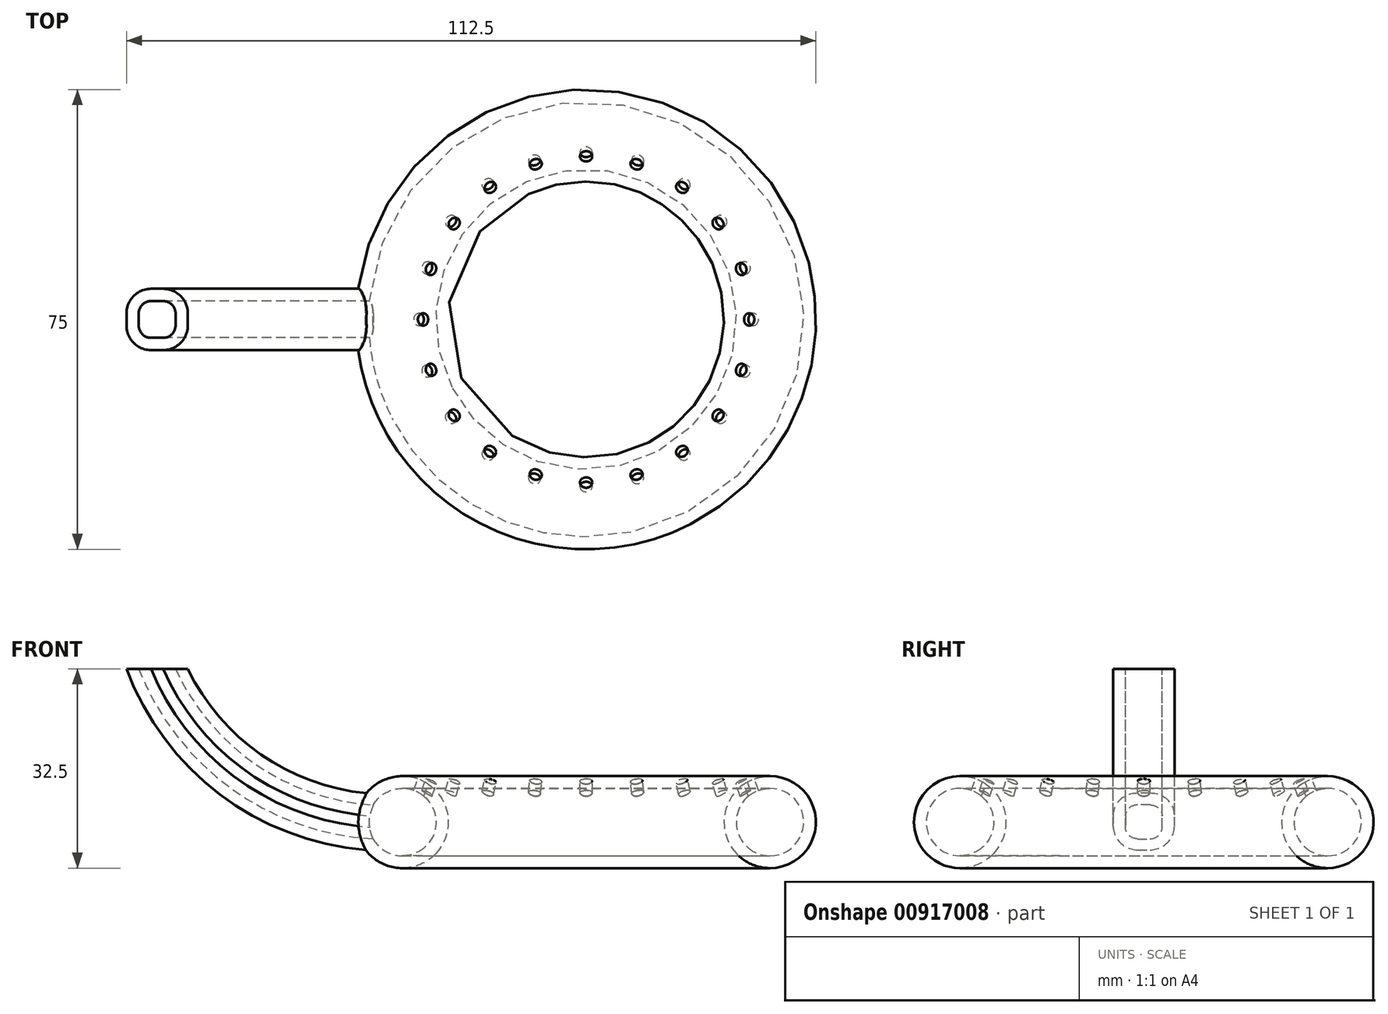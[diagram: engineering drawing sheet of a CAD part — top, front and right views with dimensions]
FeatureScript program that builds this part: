
annotation { "Feature Type Name" : "Feature", "Feature Type Description" : "" }
export const myFeature = defineFeature(function(context is Context, id is Id, definition is map)
    precondition{}
    {
        {
            var Q0;
            Q0=qCreatedBy(makeId("Front.planeOp"),FACE);
            var sketch = newSketch(context, id + "F0", { "sketchPlane" : qUnion([Q0])});
            skCircle(sketch, "E0", {"center": v(-30, 0) * mm, "radius": 7.5 * mm});
            skCircle(sketch, "E1", {"center": v(-30, 0) * mm, "radius": 5.5 * mm});
            skLineSegment(sketch, "E2", {"start": v(0, 0) * mm, "end": v(0, 9.49) * mm});
            skSolve(sketch);
        }
        {
            var Q0;
            Q0=makeQuery(id+"F0.imprint","IMPRINT",FACE,{"disambiguationData":[TD([[makeQuery(id+"F0.imprint","IMPRINT",EDGE,{"derivedFrom":sQuery(id+"F0.wireOp",EDGE,"E0")}),1.0]])]});
            var Q1;
            Q1=sQuery(id+"F0.wireOp",EDGE,"E2");
            revolve(context, id + "F1", {"surfaceOperationType" : NewSurfaceOperationType.NEW, "entities" : qUnion([Q0]), "axis" : qUnion([Q1]), "revolveType" : RevolveType.FULL});
        }
        {
            var Q0;
            Q0=qCreatedBy(makeId("Top.planeOp"),FACE);
            cPlane(context, id + "F2", {"entities" : qUnion([Q0]), "cplaneType" : CPlaneType.OFFSET, "offset" : 25 * mm, "width" : 150 * mm, "height" : 150 * mm});
        }
        {
            var Q0;
            Q0=qCreatedBy(id+"F2.planeOp",FACE);
            var sketch = newSketch(context, id + "F3", { "sketchPlane" : qUnion([Q0])});
            skLineSegment(sketch, "E3", {"start": v(0, 0) * mm, "end": v(-20, 0) * mm});
            skCircle(sketch, "E4", {"center": v(-20, 0) * mm, "radius": 1 * mm});
            skCircle(sketch, "E5.1.0", {"center": v(-19.02, -6.18) * mm, "radius": 1 * mm});
            skCircle(sketch, "E5.2.0", {"center": v(-16.18, -11.76) * mm, "radius": 1 * mm});
            skPoint(sketch, "E5.center", {"position": v(0, 0) * mm});
            skCircle(sketch, "E6.1.3.0", {"center": v(-11.76, -16.18) * mm, "radius": 1 * mm});
            skCircle(sketch, "E6.1.4.0", {"center": v(-6.18, -19.02) * mm, "radius": 1 * mm});
            skCircle(sketch, "E6.1.5.0", {"center": v(0, -20) * mm, "radius": 1 * mm});
            skCircle(sketch, "E6.1.6.0", {"center": v(6.18, -19.02) * mm, "radius": 1 * mm});
            skCircle(sketch, "E6.1.7.0", {"center": v(11.76, -16.18) * mm, "radius": 1 * mm});
            skCircle(sketch, "E6.1.8.0", {"center": v(16.18, -11.76) * mm, "radius": 1 * mm});
            skCircle(sketch, "E6.1.9.0", {"center": v(19.02, -6.18) * mm, "radius": 1 * mm});
            skCircle(sketch, "E6.1.10.0", {"center": v(20, 0) * mm, "radius": 1 * mm});
            skCircle(sketch, "E6.1.11.0", {"center": v(19.02, 6.18) * mm, "radius": 1 * mm});
            skCircle(sketch, "E6.1.12.0", {"center": v(16.18, 11.76) * mm, "radius": 1 * mm});
            skCircle(sketch, "E6.1.13.0", {"center": v(11.76, 16.18) * mm, "radius": 1 * mm});
            skCircle(sketch, "E6.1.14.0", {"center": v(6.18, 19.02) * mm, "radius": 1 * mm});
            skCircle(sketch, "E6.1.15.0", {"center": v(0, 20) * mm, "radius": 1 * mm});
            skCircle(sketch, "E6.1.16.0", {"center": v(-6.18, 19.02) * mm, "radius": 1 * mm});
            skCircle(sketch, "E6.1.17.0", {"center": v(-11.76, 16.18) * mm, "radius": 1 * mm});
            skCircle(sketch, "E6.1.18.0", {"center": v(-16.18, 11.76) * mm, "radius": 1 * mm});
            skCircle(sketch, "E6.1.19.0", {"center": v(-19.02, 6.18) * mm, "radius": 1 * mm});
            skSolve(sketch);
        }
        {
            var Q0;
            Q0=qCreatedBy(makeId("Top.planeOp"),FACE);
            var sketch = newSketch(context, id + "F4", { "sketchPlane" : qUnion([Q0])});
            skLineSegment(sketch, "E7", {"start": v(0, 0) * mm, "end": v(-29, 0) * mm});
            skCircle(sketch, "E8", {"center": v(-29, 0) * mm, "radius": 1 * mm});
            skCircle(sketch, "E9.1.0", {"center": v(-27.58, -8.96) * mm, "radius": 1 * mm});
            skCircle(sketch, "E9.2.0", {"center": v(-23.46, -17.05) * mm, "radius": 1 * mm});
            skCircle(sketch, "E9.3.0", {"center": v(-17.05, -23.46) * mm, "radius": 1 * mm});
            skCircle(sketch, "E9.4.0", {"center": v(-8.96, -27.58) * mm, "radius": 1 * mm});
            skCircle(sketch, "E9.5.0", {"center": v(0, -29) * mm, "radius": 1 * mm});
            skCircle(sketch, "E9.6.0", {"center": v(8.96, -27.58) * mm, "radius": 1 * mm});
            skCircle(sketch, "E9.7.0", {"center": v(17.05, -23.46) * mm, "radius": 1 * mm});
            skCircle(sketch, "E9.8.0", {"center": v(23.46, -17.05) * mm, "radius": 1 * mm});
            skCircle(sketch, "E9.9.0", {"center": v(27.58, -8.96) * mm, "radius": 1 * mm});
            skCircle(sketch, "E9.10.0", {"center": v(29, 0) * mm, "radius": 1 * mm});
            skCircle(sketch, "E9.11.0", {"center": v(27.58, 8.96) * mm, "radius": 1 * mm});
            skCircle(sketch, "E9.12.0", {"center": v(23.46, 17.05) * mm, "radius": 1 * mm});
            skCircle(sketch, "E9.13.0", {"center": v(17.05, 23.46) * mm, "radius": 1 * mm});
            skCircle(sketch, "E9.14.0", {"center": v(8.96, 27.58) * mm, "radius": 1 * mm});
            skCircle(sketch, "E9.15.0", {"center": v(0, 29) * mm, "radius": 1 * mm});
            skCircle(sketch, "E9.16.0", {"center": v(-8.96, 27.58) * mm, "radius": 1 * mm});
            skCircle(sketch, "E9.17.0", {"center": v(-17.05, 23.46) * mm, "radius": 1 * mm});
            skCircle(sketch, "E9.18.0", {"center": v(-23.46, 17.05) * mm, "radius": 1 * mm});
            skCircle(sketch, "E9.19.0", {"center": v(-27.58, 8.96) * mm, "radius": 1 * mm});
            skPoint(sketch, "E9.center", {"position": v(0, 0) * mm});
            skSolve(sketch);
        }
        {
            var Q0;
            Q0=makeQuery(id+"F3.imprint","IMPRINT",FACE,{"disambiguationData":[TD([[makeQuery(id+"F3.imprint","IMPRINT",EDGE,{"derivedFrom":sQuery(id+"F3.wireOp",EDGE,"E4")}),1.0]])]});
            var Q1;
            Q1=makeQuery(id+"F4.imprint","IMPRINT",FACE,{"disambiguationData":[TD([[makeQuery(id+"F4.imprint","IMPRINT",EDGE,{"derivedFrom":sQuery(id+"F4.wireOp",EDGE,"E8")}),1.0]])]});
            loft(context, id + "F5", {"sheetProfilesArray" : [{ "sheetProfileEntities" : qUnion([Q0]) }, { "sheetProfileEntities" : qUnion([Q1]) }]});
        }
        {
            var Q0;
            Q0=qCreatedBy(makeId("Front.planeOp"),FACE);
            var sketch = newSketch(context, id + "F6", { "sketchPlane" : qUnion([Q0])});
            skLineSegment(sketch, "E10", {"start": v(0, 0) * mm, "end": v(0, 24.98) * mm});
            skSolve(sketch);
        }
        {
            var Q0;
            Q0=makeQuery(id+"F5.opLoft","SWEPT_BODY",BODY,{"disambiguationData":[OSD([makeQuery(id+"F3.imprint","IMPRINT",FACE,{"disambiguationData":[TD([[makeQuery(id+"F3.imprint","IMPRINT",EDGE,{"derivedFrom":sQuery(id+"F3.wireOp",EDGE,"E4")}),1.0]])]}),makeQuery(id+"F4.imprint","IMPRINT",FACE,{"disambiguationData":[TD([[makeQuery(id+"F4.imprint","IMPRINT",EDGE,{"derivedFrom":sQuery(id+"F4.wireOp",EDGE,"E8")}),1.0]])]})])]});
            var Q1;
            Q1=sQuery(id+"F6.wireOp",EDGE,"E10");
            circularPattern(context, id + "F7", {"operationType" : NewBodyOperationType.REMOVE, "entities" : qUnion([Q0]), "axis" : qUnion([Q1]), "angle" : 360 * degree, "instanceCount" : 20, "equalSpace" : true});
        }
        {
            var Q0;
            Q0=qCreatedBy(makeId("Front.planeOp"),FACE);
            var sketch = newSketch(context, id + "F8", { "sketchPlane" : qUnion([Q0])});
            skArc(sketch, "E11", {"start": v(-70, 25) * mm, "mid": v(-54.37, 6.44) * mm, "end": v(-30.97, 0) * mm});
            skPoint(sketch, "E12.0.internal.orphan", {"position": v(-30.97, 0) * mm});
            skPoint(sketch, "E12.startDerivative.orphan", {"position": v(-39.33, 0) * mm});
            skSolve(sketch);
        }
        {
            var Q0;
            Q0=qCreatedBy(id+"F2.planeOp",FACE);
            var sketch = newSketch(context, id + "F9", { "sketchPlane" : qUnion([Q0])});
            skPoint(sketch, "E13.center.orphan", {"position": v(-70, 0) * mm});
            skLineSegment(sketch, "E14.bottom", {"start": v(-71, -3) * mm, "end": v(-69, -3) * mm});
            skLineSegment(sketch, "E14.top", {"start": v(-71, 3) * mm, "end": v(-69, 3) * mm});
            skLineSegment(sketch, "E14.left", {"start": v(-73, -1) * mm, "end": v(-73, 1) * mm});
            skLineSegment(sketch, "E14.right", {"start": v(-67, -1) * mm, "end": v(-67, 1) * mm});
            skPoint(sketch, "E15.visualSharp", {"position": v(-73, 3) * mm});
            skArc(sketch, "E15.filletArc", {"start": v(-71, 3) * mm, "mid": v(-72.41, 2.41) * mm, "end": v(-73, 1) * mm});
            skPoint(sketch, "E16.visualSharp", {"position": v(-67, 3) * mm});
            skArc(sketch, "E16.filletArc", {"start": v(-67, 1) * mm, "mid": v(-67.59, 2.41) * mm, "end": v(-69, 3) * mm});
            skPoint(sketch, "E17.visualSharp", {"position": v(-73, -3) * mm});
            skArc(sketch, "E17.filletArc", {"start": v(-73, -1) * mm, "mid": v(-72.41, -2.41) * mm, "end": v(-71, -3) * mm});
            skPoint(sketch, "E18.visualSharp", {"position": v(-67, -3) * mm});
            skArc(sketch, "E18.filletArc", {"start": v(-69, -3) * mm, "mid": v(-67.59, -2.41) * mm, "end": v(-67, -1) * mm});
            skArc(sketch, "E19.0", {"start": v(-71, 5) * mm, "mid": v(-73.83, 3.83) * mm, "end": v(-75, 1) * mm});
            skLineSegment(sketch, "E19.1", {"start": v(-75, -1) * mm, "end": v(-75, 1) * mm});
            skLineSegment(sketch, "E19.2", {"start": v(-71, 5) * mm, "end": v(-69, 5) * mm});
            skArc(sketch, "E19.3", {"start": v(-75, -1) * mm, "mid": v(-73.83, -3.83) * mm, "end": v(-71, -5) * mm});
            skArc(sketch, "E19.4", {"start": v(-65, 1) * mm, "mid": v(-66.17, 3.83) * mm, "end": v(-69, 5) * mm});
            skLineSegment(sketch, "E19.5", {"start": v(-65, -1) * mm, "end": v(-65, 1) * mm});
            skArc(sketch, "E19.6", {"start": v(-69, -5) * mm, "mid": v(-66.17, -3.83) * mm, "end": v(-65, -1) * mm});
            skLineSegment(sketch, "E19.7", {"start": v(-71, -5) * mm, "end": v(-69, -5) * mm});
            skSolve(sketch);
        }
        {
            var Q0;
            Q0=makeQuery(id+"F9.imprint","IMPRINT",FACE,{"disambiguationData":[TD([[makeQuery(id+"F9.imprint","IMPRINT",EDGE,{"derivedFrom":sQuery(id+"F9.wireOp",EDGE,"E14.bottom")}),1.0]])]});
            var Q1;
            Q1=sQuery(id+"F8.wireOp",EDGE,"E11");
            sweep(context, id + "F10", {"operationType" : NewBodyOperationType.REMOVE, "profiles" : qUnion([Q0]), "path" : qUnion([Q1])});
        }
        {
            var Q0;
            Q0=makeQuery(id+"F9.imprint","IMPRINT",FACE,{"disambiguationData":[TD([[makeQuery(id+"F9.imprint","IMPRINT",EDGE,{"derivedFrom":sQuery(id+"F9.wireOp",EDGE,"E14.bottom")}),-1.0]])]});
            var Q1;
            Q1=sQuery(id+"F8.wireOp",EDGE,"E11");
            sweep(context, id + "F11", {"operationType" : NewBodyOperationType.ADD, "profiles" : qUnion([Q0]), "path" : qUnion([Q1])});
        }
        {
            var Q0;
            Q0=makeQuery(id+"F0.imprint","IMPRINT",FACE,{"disambiguationData":[TD([[makeQuery(id+"F0.imprint","IMPRINT",EDGE,{"derivedFrom":sQuery(id+"F0.wireOp",EDGE,"E1")}),1.0]])]});
            var Q1;
            Q1=sQuery(id+"F0.wireOp",EDGE,"E2");
            revolve(context, id + "F12", {"operationType" : NewBodyOperationType.REMOVE, "surfaceOperationType" : NewSurfaceOperationType.NEW, "entities" : qUnion([Q0]), "axis" : qUnion([Q1]), "revolveType" : RevolveType.FULL, "oppositeDirection" : true});
        }
    });
